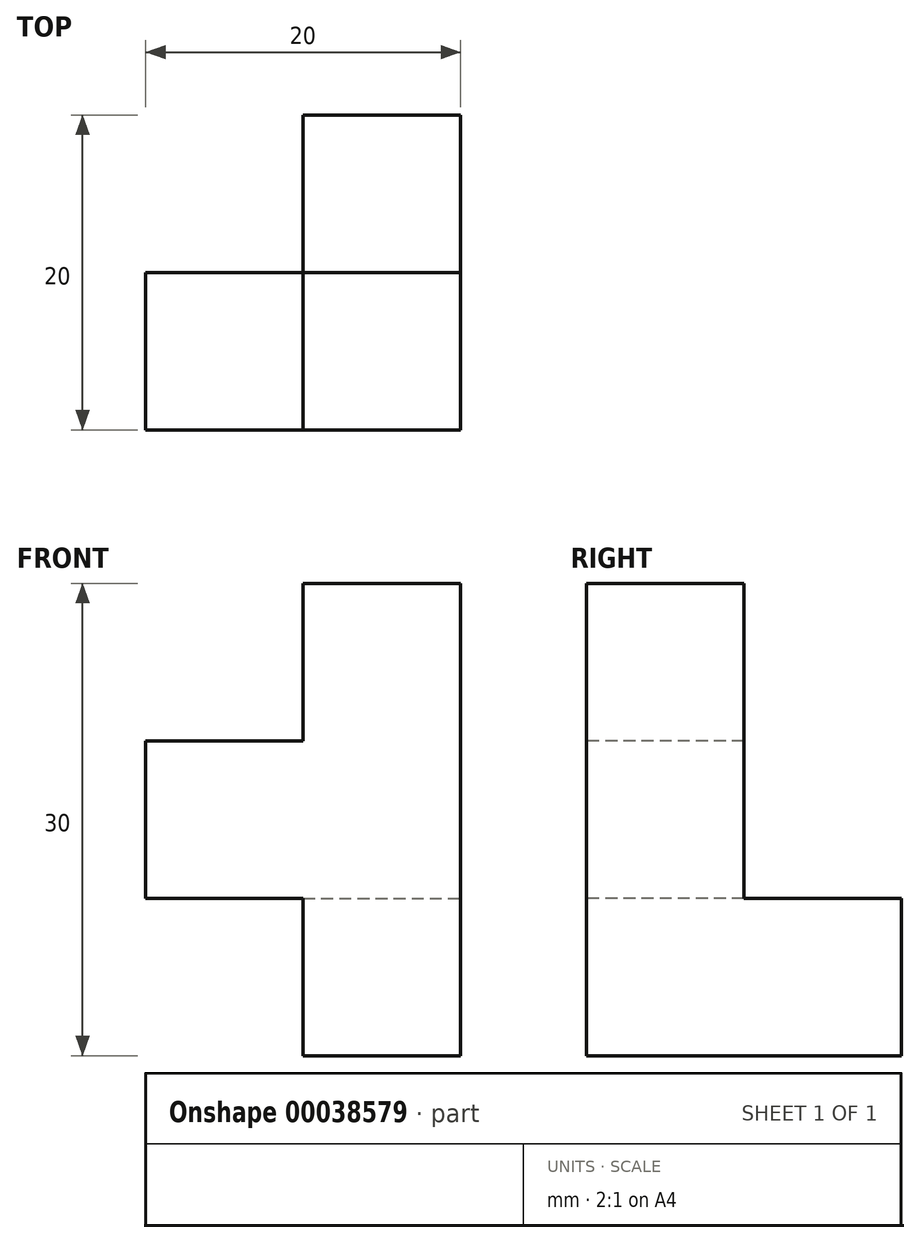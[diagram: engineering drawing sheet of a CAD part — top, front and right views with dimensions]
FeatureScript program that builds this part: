
annotation { "Feature Type Name" : "Feature", "Feature Type Description" : "" }
export const myFeature = defineFeature(function(context is Context, id is Id, definition is map)
    precondition{}
    {
        {
            var Q0;
            Q0=qCreatedBy(makeId("Top.planeOp"),FACE);
            var sketch = newSketch(context, id + "F0", { "sketchPlane" : qUnion([Q0])});
            skLineSegment(sketch, "E0.bottom", {"start": v(0, 0) * mm, "end": v(10, 0) * mm});
            skLineSegment(sketch, "E0.top", {"start": v(0, -10) * mm, "end": v(10, -10) * mm});
            skLineSegment(sketch, "E0.left", {"start": v(0, 0) * mm, "end": v(0, -10) * mm});
            skLineSegment(sketch, "E0.right", {"start": v(10, 0) * mm, "end": v(10, -10) * mm});
            skSolve(sketch);
        }
        {
            var Q0;
            Q0=makeQuery(id+"F0.imprint","IMPRINT",FACE,{"disambiguationData":[TD([[makeQuery(id+"F0.imprint","IMPRINT",EDGE,{"derivedFrom":sQuery(id+"F0.wireOp",EDGE,"E0.bottom")}),-1.0]])]});
            extrude(context, id + "F1", {"entities" : qUnion([Q0]), "depth" : 20 * mm});
        }
        {
            var Q0;
            Q0=qCreatedBy(makeId("Right.planeOp"),FACE);
            var sketch = newSketch(context, id + "F2", { "sketchPlane" : qUnion([Q0])});
            skLineSegment(sketch, "E1.bottom", {"start": v(0, 0) * mm, "end": v(-10, 0) * mm});
            skLineSegment(sketch, "E1.top", {"start": v(0, 10) * mm, "end": v(-10, 10) * mm});
            skLineSegment(sketch, "E1.left", {"start": v(0, 0) * mm, "end": v(0, 10) * mm});
            skLineSegment(sketch, "E1.right", {"start": v(-10, 0) * mm, "end": v(-10, 10) * mm});
            skSolve(sketch);
        }
        {
            var Q0;
            Q0=makeQuery(id+"F2.imprint","IMPRINT",FACE,{"disambiguationData":[TD([[makeQuery(id+"F2.imprint","IMPRINT",EDGE,{"derivedFrom":sQuery(id+"F2.wireOp",EDGE,"E1.bottom")}),-1.0]])]});
            extrude(context, id + "F3", {"entities" : qUnion([Q0]), "operationType" : NewBodyOperationType.ADD, "depth" : 10 * mm});
        }
        {
            var Q0;
            Q0=qCreatedBy(makeId("Right.planeOp"),FACE);
            var sketch = newSketch(context, id + "F4", { "sketchPlane" : qUnion([Q0])});
            skLineSegment(sketch, "E2.bottom", {"start": v(0, 0) * mm, "end": v(-10, 0) * mm});
            skLineSegment(sketch, "E2.top", {"start": v(0, 10) * mm, "end": v(-10, 10) * mm});
            skLineSegment(sketch, "E2.left", {"start": v(0, 0) * mm, "end": v(0, 10) * mm});
            skLineSegment(sketch, "E2.right", {"start": v(-10, 0) * mm, "end": v(-10, 10) * mm});
            skSolve(sketch);
        }
        {
            var Q0;
            Q0=makeQuery(id+"F4.imprint","IMPRINT",FACE,{"disambiguationData":[TD([[makeQuery(id+"F4.imprint","IMPRINT",EDGE,{"derivedFrom":sQuery(id+"F4.wireOp",EDGE,"E2.bottom")}),-1.0]])]});
            extrude(context, id + "F5", {"entities" : qUnion([Q0]), "operationType" : NewBodyOperationType.ADD, "oppositeDirection" : true, "depth" : 10 * mm});
        }
        {
            var Q0;
            Q0=makeQuery(id+"F5.boolean.opBoolean","MERGE",FACE,{"derivedFrom":[makeQuery(id+"F1.opExtrude","CAP_FACE",FACE,{"disambiguationData":[OSD([sQuery(id+"F0.wireOp",EDGE,"E0.bottom"),sQuery(id+"F0.wireOp",EDGE,"E0.top"),sQuery(id+"F0.wireOp",EDGE,"E0.left"),sQuery(id+"F0.wireOp",EDGE,"E0.right")])],"isStart":true}),makeQuery(id+"F5.opExtrude","SWEPT_FACE",FACE,{"disambiguationData":[OSD([sQuery(id+"F4.wireOp",EDGE,"E2.bottom")])]})]});
            var sketch = newSketch(context, id + "F6", { "sketchPlane" : qUnion([Q0])});
            skLineSegment(sketch, "E3", {"start": v(0, 0) * mm, "end": v(0, 10) * mm});
            skSolve(sketch);
        }
        {
            var Q0;
            {var subQ2=sQuery(id+"F6.wireOp",EDGE,"E3");Q0=makeQuery(id+"F6.imprint","IMPRINT",FACE,{"disambiguationData":[TD([[makeQuery(id+"F6.imprint","IMPRINT",EDGE,{"derivedFrom":subQ2}),-1.0]])]});}
            extrude(context, id + "F7", {"entities" : qUnion([Q0]), "operationType" : NewBodyOperationType.ADD, "depth" : 10 * mm});
        }
        {
            var Q0;
            Q0=qCreatedBy(makeId("Front.planeOp"),FACE);
            var sketch = newSketch(context, id + "F8", { "sketchPlane" : qUnion([Q0])});
            skLineSegment(sketch, "E4.bottom", {"start": v(0, 0) * mm, "end": v(10, 0) * mm});
            skLineSegment(sketch, "E4.top", {"start": v(0, -10) * mm, "end": v(10, -10) * mm});
            skLineSegment(sketch, "E4.left", {"start": v(0, 0) * mm, "end": v(0, -10) * mm});
            skLineSegment(sketch, "E4.right", {"start": v(10, 0) * mm, "end": v(10, -10) * mm});
            skSolve(sketch);
        }
        {
            var Q0;
            Q0=makeQuery(id+"F8.imprint","IMPRINT",FACE,{"disambiguationData":[TD([[makeQuery(id+"F8.imprint","IMPRINT",EDGE,{"derivedFrom":sQuery(id+"F8.wireOp",EDGE,"E4.bottom")}),-1.0]])]});
            extrude(context, id + "F9", {"entities" : qUnion([Q0]), "operationType" : NewBodyOperationType.ADD, "oppositeDirection" : true, "depth" : 10 * mm});
        }
    });
